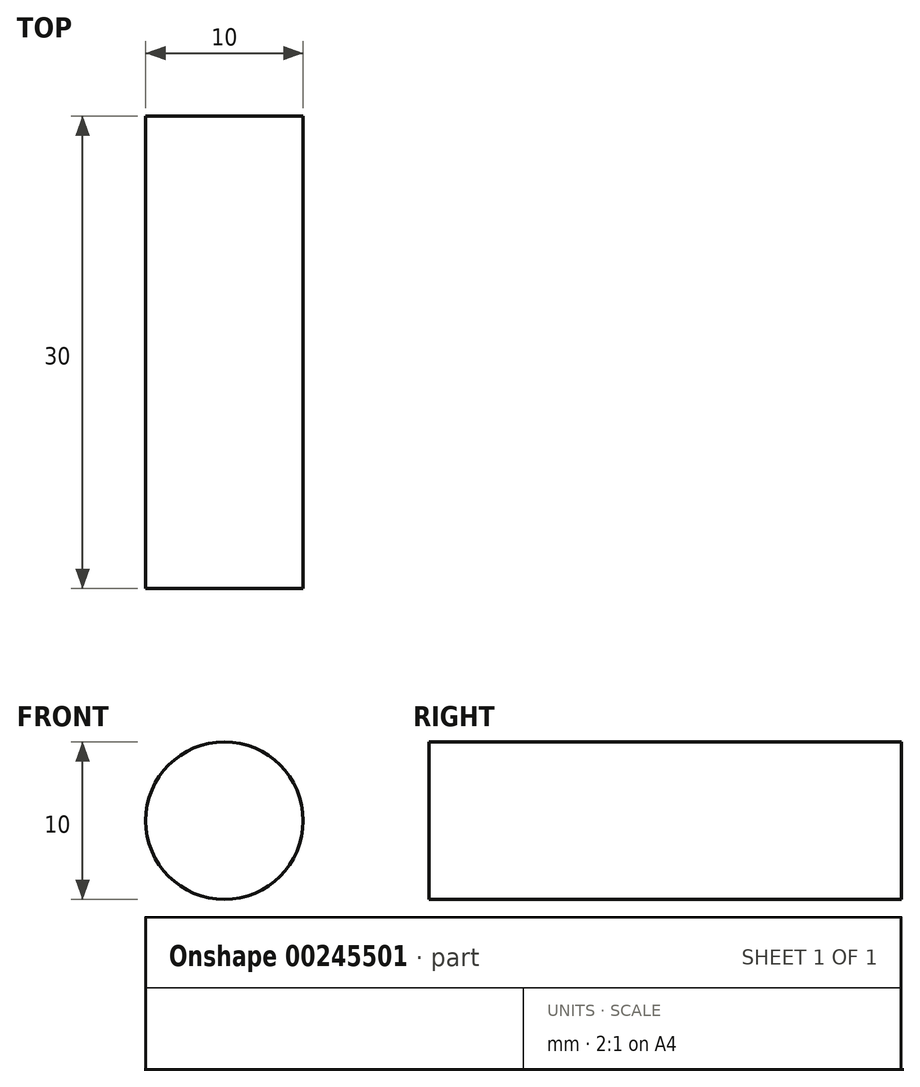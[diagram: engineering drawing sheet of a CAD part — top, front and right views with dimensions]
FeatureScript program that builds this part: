
annotation { "Feature Type Name" : "Feature", "Feature Type Description" : "" }
export const myFeature = defineFeature(function(context is Context, id is Id, definition is map)
    precondition{}
    {
        {
            var Q0;
            Q0=qCreatedBy(makeId("Front.planeOp"),FACE);
            var sketch = newSketch(context, id + "F0", { "sketchPlane" : qUnion([Q0])});
            skCircle(sketch, "E0", {"center": v(0, 0) * mm, "radius": 5 * mm});
            skSolve(sketch);
        }
        {
            var Q0;
            Q0=makeQuery(id+"F0.imprint","IMPRINT",FACE,{"disambiguationData":[TD([[makeQuery(id+"F0.imprint","IMPRINT",EDGE,{"derivedFrom":sQuery(id+"F0.wireOp",EDGE,"E0")}),1.0]])]});
            extrude(context, id + "F1", {"entities" : qUnion([Q0]), "depth" : 30 * mm});
        }
    });
